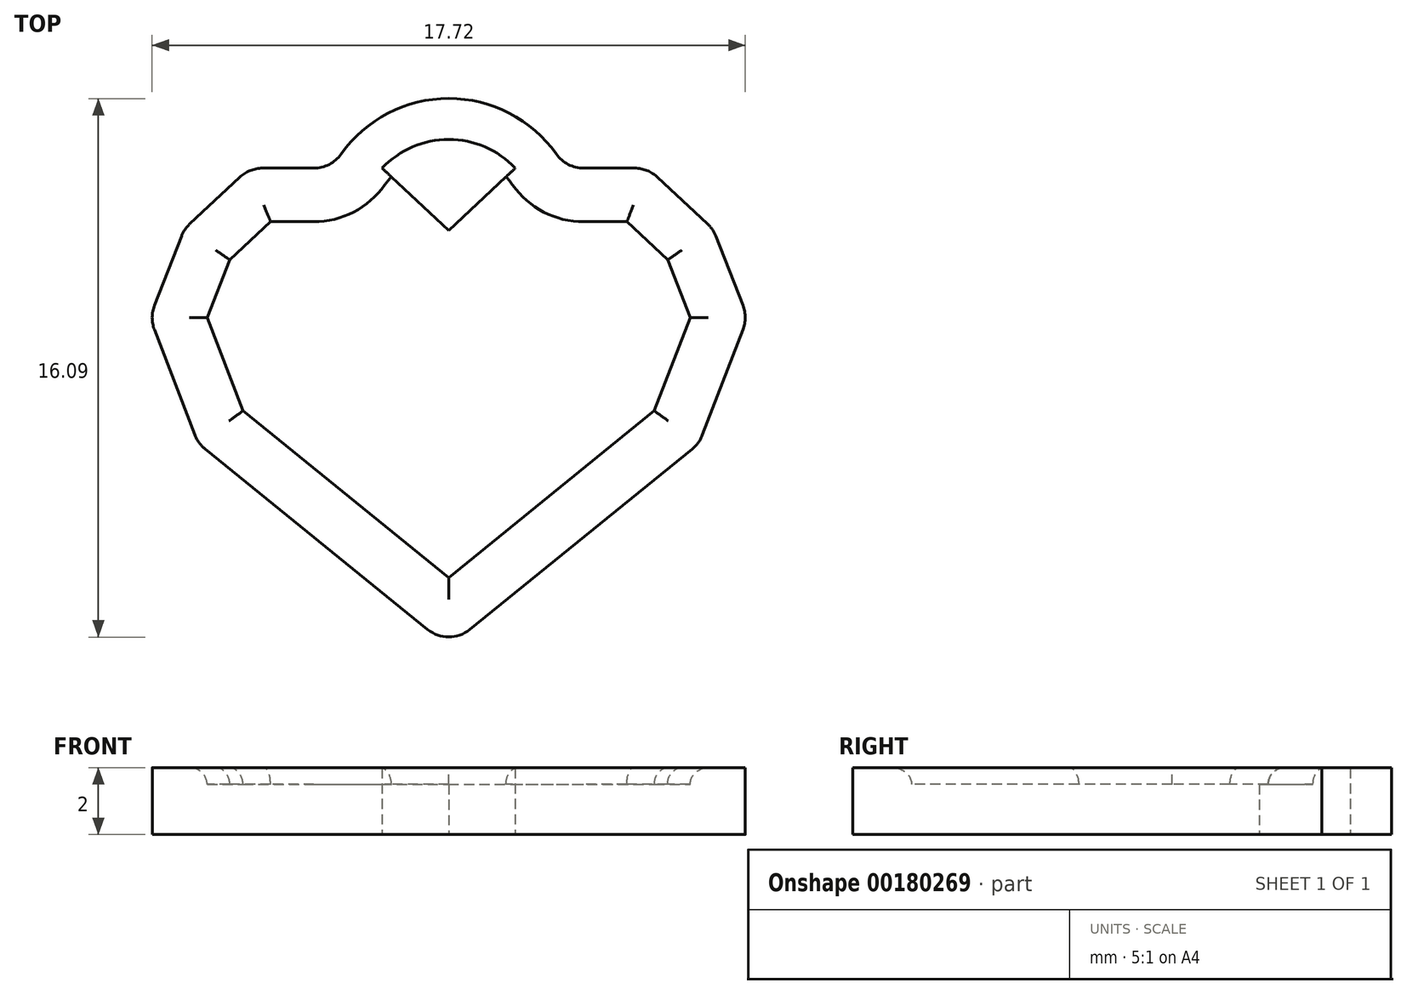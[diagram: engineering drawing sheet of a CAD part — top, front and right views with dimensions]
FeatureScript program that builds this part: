
annotation { "Feature Type Name" : "Feature", "Feature Type Description" : "" }
export const myFeature = defineFeature(function(context is Context, id is Id, definition is map)
    precondition{}
    {
        {
            var Q0;
            Q0=qCreatedBy(makeId("Top.planeOp"),FACE);
            var sketch = newSketch(context, id + "F0", { "sketchPlane" : qUnion([Q0])});
            skLineSegment(sketch, "E0", {"start": v(0, 7.5) * mm, "end": v(1.99, 9.35) * mm});
            skLineSegment(sketch, "E1", {"start": v(1.99, 9.35) * mm, "end": v(5.95, 9.35) * mm});
            skLineSegment(sketch, "E2", {"start": v(5.95, 9.35) * mm, "end": v(7.9, 7.53) * mm});
            skLineSegment(sketch, "E3", {"start": v(7.9, 7.53) * mm, "end": v(8.93, 4.89) * mm});
            skLineSegment(sketch, "E4", {"start": v(8.93, 4.89) * mm, "end": v(7.48, 1.13) * mm});
            skLineSegment(sketch, "E5", {"start": v(7.48, 1.13) * mm, "end": v(0, -4.94) * mm});
            skLineSegment(sketch, "E6.MirrorCS", {"start": v(-7.48, 1.13) * mm, "end": v(0, -4.94) * mm});
            skLineSegment(sketch, "E7.MirrorCS", {"start": v(0, 7.5) * mm, "end": v(-1.99, 9.35) * mm});
            skLineSegment(sketch, "E8.MirrorCS", {"start": v(-8.93, 4.89) * mm, "end": v(-7.48, 1.13) * mm});
            skLineSegment(sketch, "E9.MirrorCS", {"start": v(-5.95, 9.35) * mm, "end": v(-7.9, 7.53) * mm});
            skLineSegment(sketch, "E10.MirrorCS", {"start": v(-1.99, 9.35) * mm, "end": v(-5.95, 9.35) * mm});
            skLineSegment(sketch, "E11.MirrorCS", {"start": v(-7.9, 7.53) * mm, "end": v(-8.93, 4.89) * mm});
            skCircle(sketch, "E12", {"center": v(0, 7.5) * mm, "radius": 2.72 * mm});
            skCircle(sketch, "E13", {"center": v(0, 7.5) * mm, "radius": 3.94 * mm});
            skSolve(sketch);
        }
        {
            var Q0;
            {var subQ1=sQuery(id+"F0.wireOp",EDGE,"E1");var subQ3=sQuery(id+"F0.wireOp",EDGE,"E13");var subQ4=makeQuery(id+"F0.imprint","INTERSECT",VERTEX,{"derivedFrom":[subQ1,subQ3]});Q0=makeQuery(id+"F0.imprint","IMPRINT",FACE,{"disambiguationData":[TD([[makeQuery(id+"F0.imprint","IMPRINT",EDGE,{"disambiguationData":[TD([[subQ4,-1.0]])],"derivedFrom":subQ3}),1.0]])]});}
            var Q1;
            {var subQ0=sQuery(id+"F0.wireOp",EDGE,"E2");Q1=makeQuery(id+"F0.imprint","IMPRINT",FACE,{"disambiguationData":[TD([[makeQuery(id+"F0.imprint","IMPRINT",EDGE,{"derivedFrom":subQ0}),-1.0]])]});}
            var Q2;
            {var subQ1=sQuery(id+"F0.wireOp",EDGE,"E1");var subQ3=sQuery(id+"F0.wireOp",EDGE,"E13");var subQ4=makeQuery(id+"F0.imprint","INTERSECT",VERTEX,{"derivedFrom":[subQ1,subQ3]});Q2=makeQuery(id+"F0.imprint","IMPRINT",FACE,{"disambiguationData":[TD([[makeQuery(id+"F0.imprint","IMPRINT",EDGE,{"disambiguationData":[TD([[subQ4,1.0]])],"derivedFrom":subQ3}),1.0]])]});}
            var Q3;
            {var subQ0=sQuery(id+"F0.wireOp",EDGE,"E0");Q3=makeQuery(id+"F0.imprint","IMPRINT",FACE,{"disambiguationData":[TD([[makeQuery(id+"F0.imprint","IMPRINT",EDGE,{"derivedFrom":subQ0}),-1.0]])]});}
            extrude(context, id + "F1", {"entities" : qUnion([Q0, Q1, Q2, Q3]), "depth" : 1.5 * mm});
        }
        {
            var Q0;
            Q0=makeQuery(id+"F1.opExtrude","SWEPT_EDGE",EDGE,{"disambiguationData":[OSD([sQuery(id+"F0.wireOp",EDGE,"E5"),sQuery(id+"F0.wireOp",EDGE,"E6.MirrorCS")])]});
            fillet(context, id + "F2", {"entities" : qUnion([Q0]), "radius" : 1 * mm, "tangentPropagation" : true, "allowEdgeOverflow" : false});
        }
        {
            var Q0;
            Q0=makeQuery(id+"F1.opExtrude","SWEPT_EDGE",EDGE,{"disambiguationData":[OSD([sQuery(id+"F0.wireOp",EDGE,"E4"),sQuery(id+"F0.wireOp",EDGE,"E5")])]});
            var Q1;
            Q1=makeQuery(id+"F1.opExtrude","SWEPT_EDGE",EDGE,{"disambiguationData":[OSD([sQuery(id+"F0.wireOp",EDGE,"E3"),sQuery(id+"F0.wireOp",EDGE,"E4")])]});
            var Q2;
            Q2=makeQuery(id+"F1.opExtrude","SWEPT_EDGE",EDGE,{"disambiguationData":[OSD([sQuery(id+"F0.wireOp",EDGE,"E2"),sQuery(id+"F0.wireOp",EDGE,"E3")])]});
            var Q3;
            Q3=makeQuery(id+"F1.opExtrude","SWEPT_EDGE",EDGE,{"disambiguationData":[OSD([sQuery(id+"F0.wireOp",EDGE,"E1"),sQuery(id+"F0.wireOp",EDGE,"E2")])]});
            var Q4;
            Q4=makeQuery(id+"F1.opExtrude","SWEPT_EDGE",EDGE,{"disambiguationData":[OSD([sQuery(id+"F0.wireOp",EDGE,"E6.MirrorCS"),sQuery(id+"F0.wireOp",EDGE,"E8.MirrorCS")])]});
            var Q5;
            Q5=makeQuery(id+"F1.opExtrude","SWEPT_EDGE",EDGE,{"disambiguationData":[OSD([sQuery(id+"F0.wireOp",EDGE,"E8.MirrorCS"),sQuery(id+"F0.wireOp",EDGE,"E11.MirrorCS")])]});
            var Q6;
            Q6=makeQuery(id+"F1.opExtrude","SWEPT_EDGE",EDGE,{"disambiguationData":[OSD([sQuery(id+"F0.wireOp",EDGE,"E9.MirrorCS"),sQuery(id+"F0.wireOp",EDGE,"E11.MirrorCS")])]});
            var Q7;
            Q7=makeQuery(id+"F1.opExtrude","SWEPT_EDGE",EDGE,{"disambiguationData":[OSD([sQuery(id+"F0.wireOp",EDGE,"E9.MirrorCS"),sQuery(id+"F0.wireOp",EDGE,"E10.MirrorCS")])]});
            var Q8;
            Q8=makeQuery(id+"F1.opExtrude","SWEPT_EDGE",EDGE,{"disambiguationData":[OSD([sQuery(id+"F0.wireOp",EDGE,"E10.MirrorCS"),sQuery(id+"F0.wireOp",EDGE,"E13")])]});
            var Q9;
            Q9=makeQuery(id+"F1.opExtrude","SWEPT_EDGE",EDGE,{"disambiguationData":[OSD([sQuery(id+"F0.wireOp",EDGE,"E1"),sQuery(id+"F0.wireOp",EDGE,"E13")])]});
            fillet(context, id + "F3", {"entities" : qUnion([Q0, Q1, Q2, Q3, Q4, Q5, Q6, Q7, Q8, Q9]), "radius" : 1 * mm, "tangentPropagation" : true, "allowEdgeOverflow" : false});
        }
        {
            var Q0;
            Q0=makeQuery(id+"F1.opExtrude","CAP_FACE",FACE,{"disambiguationData":[OSD([sQuery(id+"F0.wireOp",EDGE,"E0"),sQuery(id+"F0.wireOp",EDGE,"E1"),sQuery(id+"F0.wireOp",EDGE,"E2"),sQuery(id+"F0.wireOp",EDGE,"E3"),sQuery(id+"F0.wireOp",EDGE,"E4"),sQuery(id+"F0.wireOp",EDGE,"E5"),sQuery(id+"F0.wireOp",EDGE,"E6.MirrorCS"),sQuery(id+"F0.wireOp",EDGE,"E7.MirrorCS"),sQuery(id+"F0.wireOp",EDGE,"E8.MirrorCS"),sQuery(id+"F0.wireOp",EDGE,"E9.MirrorCS"),sQuery(id+"F0.wireOp",EDGE,"E10.MirrorCS"),sQuery(id+"F0.wireOp",EDGE,"E11.MirrorCS"),sQuery(id+"F0.wireOp",EDGE,"E12"),sQuery(id+"F0.wireOp",EDGE,"E13")])],"isStart":false});
            var sketch = newSketch(context, id + "F4", { "sketchPlane" : qUnion([Q0])});
            skArc(sketch, "E14.0", {"start": v(-1.91, 8.85) * mm, "mid": v(-2.84, 8.04) * mm, "end": v(-4.03, 7.75) * mm});
            skArc(sketch, "E14.1", {"start": v(1.91, 8.85) * mm, "mid": v(0, 9.83) * mm, "end": v(-1.91, 8.85) * mm});
            skLineSegment(sketch, "E14.2", {"start": v(-6.14, 2.1) * mm, "end": v(0, -2.88) * mm});
            skLineSegment(sketch, "E14.3", {"start": v(-7.21, 4.89) * mm, "end": v(-6.14, 2.1) * mm});
            skLineSegment(sketch, "E14.4", {"start": v(-6.54, 6.61) * mm, "end": v(-7.21, 4.89) * mm});
            skLineSegment(sketch, "E14.5", {"start": v(-5.32, 7.75) * mm, "end": v(-6.54, 6.61) * mm});
            skLineSegment(sketch, "E14.6", {"start": v(0, -2.88) * mm, "end": v(6.14, 2.1) * mm});
            skLineSegment(sketch, "E14.7", {"start": v(6.14, 2.1) * mm, "end": v(7.21, 4.89) * mm});
            skLineSegment(sketch, "E14.8", {"start": v(-4.03, 7.75) * mm, "end": v(-5.32, 7.75) * mm});
            skLineSegment(sketch, "E14.9", {"start": v(7.21, 4.89) * mm, "end": v(6.54, 6.61) * mm});
            skLineSegment(sketch, "E14.10", {"start": v(6.54, 6.61) * mm, "end": v(5.32, 7.75) * mm});
            skLineSegment(sketch, "E14.11", {"start": v(5.32, 7.75) * mm, "end": v(4.03, 7.75) * mm});
            skArc(sketch, "E14.12", {"start": v(4.03, 7.75) * mm, "mid": v(2.84, 8.04) * mm, "end": v(1.91, 8.85) * mm});
            skSolve(sketch);
        }
        {
            var Q0;
            {var subQ0=sQuery(id+"F4.wireOp",EDGE,"E14.0");Q0=makeQuery(id+"F4.imprint","IMPRINT",FACE,{"disambiguationData":[TD([[makeQuery(id+"F4.imprint","IMPRINT",EDGE,{"derivedFrom":subQ0}),1.0]])]});}
            extrude(context, id + "F5", {"entities" : qUnion([Q0]), "operationType" : NewBodyOperationType.ADD, "depth" : 0.5 * mm});
        }
        {
            var Q0;
            Q0=makeQuery(id+"F5.opExtrude","CAP_EDGE",EDGE,{"disambiguationData":[OSD([sQuery(id+"F4.wireOp",EDGE,"E14.5")])],"isStart":false});
            var Q1;
            Q1=makeQuery(id+"F5.opExtrude","CAP_EDGE",EDGE,{"disambiguationData":[OSD([sQuery(id+"F4.wireOp",EDGE,"E14.4")])],"isStart":false});
            var Q2;
            Q2=makeQuery(id+"F5.opExtrude","CAP_EDGE",EDGE,{"disambiguationData":[OSD([sQuery(id+"F4.wireOp",EDGE,"E14.3")])],"isStart":false});
            var Q3;
            Q3=makeQuery(id+"F5.opExtrude","CAP_EDGE",EDGE,{"disambiguationData":[OSD([sQuery(id+"F4.wireOp",EDGE,"E14.2")])],"isStart":false});
            var Q4;
            Q4=makeQuery(id+"F5.opExtrude","CAP_EDGE",EDGE,{"disambiguationData":[OSD([sQuery(id+"F4.wireOp",EDGE,"E14.6")])],"isStart":false});
            var Q5;
            Q5=makeQuery(id+"F5.opExtrude","CAP_EDGE",EDGE,{"disambiguationData":[OSD([sQuery(id+"F4.wireOp",EDGE,"E14.7")])],"isStart":false});
            var Q6;
            Q6=makeQuery(id+"F5.opExtrude","CAP_EDGE",EDGE,{"disambiguationData":[OSD([sQuery(id+"F4.wireOp",EDGE,"E14.9")])],"isStart":false});
            var Q7;
            Q7=makeQuery(id+"F5.opExtrude","CAP_EDGE",EDGE,{"disambiguationData":[OSD([sQuery(id+"F4.wireOp",EDGE,"E14.10")])],"isStart":false});
            var Q8;
            Q8=makeQuery(id+"F5.opExtrude","CAP_EDGE",EDGE,{"disambiguationData":[OSD([sQuery(id+"F4.wireOp",EDGE,"E14.11")])],"isStart":false});
            var Q9;
            Q9=makeQuery(id+"F5.opExtrude","CAP_EDGE",EDGE,{"disambiguationData":[OSD([sQuery(id+"F4.wireOp",EDGE,"E14.12")])],"isStart":false});
            var Q10;
            Q10=makeQuery(id+"F5.opExtrude","CAP_EDGE",EDGE,{"disambiguationData":[OSD([sQuery(id+"F4.wireOp",EDGE,"E14.0")])],"isStart":false});
            fillet(context, id + "F6", {"entities" : qUnion([Q0, Q1, Q2, Q3, Q4, Q5, Q6, Q7, Q8, Q9, Q10]), "radius" : 0.5 * mm, "tangentPropagation" : true, "allowEdgeOverflow" : false});
        }
    });
